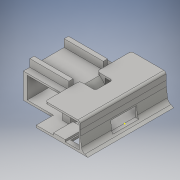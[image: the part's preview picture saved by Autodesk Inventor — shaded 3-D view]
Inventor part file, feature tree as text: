
AUTODESK INVENTOR PART (.ipt)
format: ipt  version: 2016 (Build 200138000, 138)  size: 440,320 bytes
history: native  units: in
note: dims shown in document units (in); Inventor stores cm internally (conversion verified against a paired STEP export)
features: sketch x33, extrude x31, fillet x6, chamfer x1
ambient origin geometry x8: Origin, YZ Plane, XZ Plane, XY Plane, X Axis, Y Axis, Z Axis, Center Point
bodies: Solid1 (feature_tree)
feature tree (71):
  extrude  "Extrusion1"  Depth=2.0in
  extrude  "Extrusion2"  Depth=0.4in
  extrude  "Extrusion3"  Depth=0.4in
  extrude  "Extrusion4"  Depth=0.2in
  extrude  "Extrusion5"  Depth=0.3in
  extrude  "Extrusion6"  Depth=0.2in
  extrude  "Extrusion7"  Depth=0.1in
  extrude  "Extrusion8"  Depth=0.25in TaperAngle=0.0deg
  extrude  "Extrusion9"  Depth=1.2in
  extrude  "Extrusion10"  Depth=0.25in TaperAngle=0.0deg
  extrude  "Extrusion11"  Depth=0.25in TaperAngle=0.0deg
  extrude  "Extrusion12"  Depth=1.2in
  extrude  "Extrusion13"  Depth=0.25in TaperAngle=0.0deg
  fillet  "Fillet1"  Radius=0.5in
  extrude  "Extrusion14"  Depth=6.375in TaperAngle=0.0deg
  sketch  "Sketch15"  dims[d37=0.15in d38=0.25in d39=0.0in]
  sketch  "Sketch16"  dims[d40=0.2in d41=0.5625in d42=0.0in]
  extrude  "Extrusion15"  Depth=0.25in TaperAngle=0.0deg
  extrude  "Extrusion16"  Depth=0.2in TaperAngle=0.0deg
  extrude  "Extrusion17"  Depth=0.25in TaperAngle=0.0deg
  extrude  "Extrusion18"  Depth=0.5in
  extrude  "Extrusion19"  Depth=0.15in
  extrude  "Extrusion20"  Depth=2.6875in TaperAngle=0.0deg
  extrude  "Extrusion21"  Depth=0.35in
  extrude  "Extrusion22"  Depth=0.6in
  extrude  "Extrusion23"  Depth=0.7in
  extrude  "Extrusion24"  Depth=0.275in
  extrude  "Extrusion25"  Depth=0.045in TaperAngle=0.0deg
  extrude  "Extrusion26"  Depth=0.045in TaperAngle=0.0deg
  fillet  "Fillet3"  Radius=0.45in
  extrude  "Extrusion27"  TaperAngle=0.0deg  [1 undecoded]
  extrude  "Extrusion28"  Depth=0.045in TaperAngle=0.0deg
  extrude  "Extrusion29"  Depth=0.25in TaperAngle=0.0deg
  extrude  "Extrusion30"  Depth=0.1in
  chamfer  "Chamfer1"  Distance=1.71in
  fillet  "Fillet4"  Radius=0.08in
  fillet  "Fillet5"  Radius=3.04in
  fillet  "Fillet6"  [1 undecoded]
  fillet  "Fillet7"  Radius=0.65in
  extrude  "Extrusion31"  Depth=0.05in TaperAngle=0.0deg
  sketch  "Sketch1"  dims[d0=2.0in d1=2.0in]
  sketch  "Sketch2"  dims[d2=0.8in d3=0.4in]
  sketch  "Sketch3"  dims[d4=1.0in d5=0.4in]
  sketch  "Sketch4"  dims[d6=0.05in d7=0.0in d8=0.2in]
  sketch  "Sketch5"  dims[d9=0.2in d10=0.3in]
  sketch  "Sketch6"  dims[d11=0.1in d12=0.2in]
  sketch  "Sketch7"  dims[d13=0.2in d14=0.1in]
  sketch  "Sketch8"  dims[d15=0.7in d16=0.0in d17=0.25in d18=0.0in]
  sketch  "Sketch9"  dims[d19=0.42in d20=1.2in]
  sketch  "Sketch10"  dims[d21=0.19in d22=0.25in d23=0.0in]
  sketch  "Sketch11"  dims[d24=0.5in d25=0.25in d26=0.0in]
  sketch  "Sketch12"  dims[d27=0.45in d28=1.2in]
  sketch  "Sketch13"  dims[d29=0.0in d30=0.25in d31=0.0in d32=0.5in]
  sketch  "Sketch14"  dims[d33=6.375in d34=0.0in d35=6.375in d36=0.0in]
  sketch  "Sketch17"  dims[d43=0.1in d44=0.25in d45=0.0in]
  sketch  "Sketch18"  dims[d46=0.2in d47=0.5in]
  sketch  "Sketch19"  dims[d48=2.0in d49=0.0in d50=0.15in]
  sketch  "Sketch20"  dims[d51=1.0857in d52=2.6875in d53=0.0in]
  sketch  "Sketch21"  dims[d54=0.125in d55=0.35in]
  sketch  "Sketch22"  dims[d56=4.375in d57=0.0in d58=0.6in]
  sketch  "Sketch23"  dims[d59=0.25in d60=0.7in]
  sketch  "Sketch24"  dims[d61=1.25in d62=0.0in d63=0.275in]
  sketch  "Sketch25"  dims[d64=0.4in d65=0.045in d66=0.0in]
  sketch  "Sketch26"  dims[d67=0.05in d68=0.045in d69=0.0in d70=0.45in]
  sketch  "Sketch27"  dims[d71=0.0in d72=0.0in]
  sketch  "Sketch28"  dims[d73=0.0in d74=0.045in d75=0.0in]
  sketch  "Sketch29"  dims[d76=0.25in d77=0.0in d78=0.25in d79=0.0in]
  sketch  "Sketch30"  dims[d80=0.04in d81=0.0in d82=0.1in]
  sketch  "Sketch31"  dims[d83=0.0in d84=1.71in d85=0.0in d86=0.08in d87=3.04in d88=0.0in d91=0.0in d92=0.65in d93=0.0in]
  sketch  "Sketch32"  dims[d94=0.808in d95=0.05in d96=0.0in]
  sketch  "Sketch33"  dims[d97=0.3in d98=0.0in d99=1.0in d100=0.1in d101=0.0in d102=0.06in d103=2.65in d104=0.0in d105=1.6in d106=0.0in d107=0.75in d108=0.4in d109=0.05in d110=0.0in d111=0.125in d112=0.125in d113=45.0deg d114=0.05in d115=0.05in d116=0.05in d117=0.05in d118=0.1in d119=0.9in d120=0.1in d121=0.15in d122=0.91in d123=0.15in d124=0.175in d125=0.0in]
note: 2 required parameter values undecoded (feature->parameter linkage not recoverable at this tier; creation-order binding heuristic only, values carry confidence <= 0.55)
